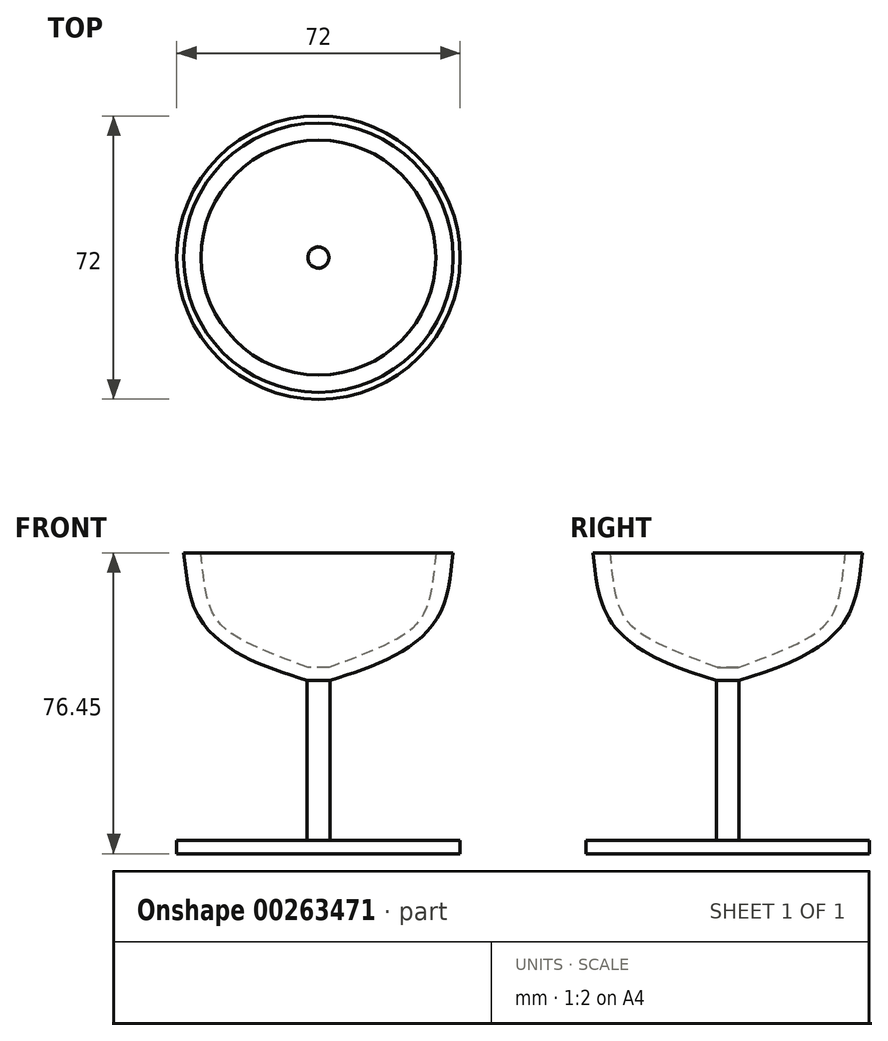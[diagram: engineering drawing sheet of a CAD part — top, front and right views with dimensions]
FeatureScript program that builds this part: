
annotation { "Feature Type Name" : "Feature", "Feature Type Description" : "" }
export const myFeature = defineFeature(function(context is Context, id is Id, definition is map)
    precondition{}
    {
        {
            var Q0;
            Q0=qCreatedBy(makeId("Front.planeOp"),FACE);
            var sketch = newSketch(context, id + "F0", { "sketchPlane" : qUnion([Q0])});
            skLineSegment(sketch, "E0", {"start": v(0, 0) * mm, "end": v(-36, 0) * mm});
            skLineSegment(sketch, "E1", {"start": v(-36, 0) * mm, "end": v(-36, 3.33) * mm});
            skLineSegment(sketch, "E2", {"start": v(-36, 3.33) * mm, "end": v(-2.89, 3.33) * mm});
            skLineSegment(sketch, "E3", {"start": v(-2.89, 3.33) * mm, "end": v(-2.89, 44) * mm});
            skFitSpline(sketch, "E4", {"points": [v(-2.89, 44) * mm, v(-19.11, 50.23) * mm, v(-30.45, 60.23) * mm, v(-34.23, 76.45) * mm], "startDerivative": vector(-48.88, 15.66) * mm, "endDerivative": vector(-5.44, 52.02) * mm});
            skPoint(sketch, "E5.start.orphan", {"position": v(0, 76.45) * mm});
            skLineSegment(sketch, "E6", {"start": v(-34.23, 76.45) * mm, "end": v(-29.83, 76.45) * mm});
            skFitSpline(sketch, "E7", {"points": [v(-29.83, 76.45) * mm, v(-26.71, 60.9) * mm, v(-18.92, 54) * mm, v(-2.67, 47.32) * mm], "startDerivative": vector(4.57, -49.97) * mm, "endDerivative": vector(47.91, -17.65) * mm});
            skLineSegment(sketch, "E8", {"start": v(-2.67, 47.32) * mm, "end": v(0, 47.32) * mm});
            skLineSegment(sketch, "E9", {"start": v(0, 47.32) * mm, "end": v(0, 0) * mm});
            skSolve(sketch);
        }
        {
            var Q0;
            Q0=makeQuery(id+"F0.imprint","IMPRINT",FACE,{"disambiguationData":[TD([[makeQuery(id+"F0.imprint","IMPRINT",EDGE,{"derivedFrom":sQuery(id+"F0.wireOp",EDGE,"E0")}),-1.0]])]});
            var Q1;
            Q1=sQuery(id+"F0.wireOp",EDGE,"E9");
            revolve(context, id + "F1", {"entities" : qUnion([Q0]), "axis" : qUnion([Q1]), "revolveType" : RevolveType.FULL});
        }
    });
